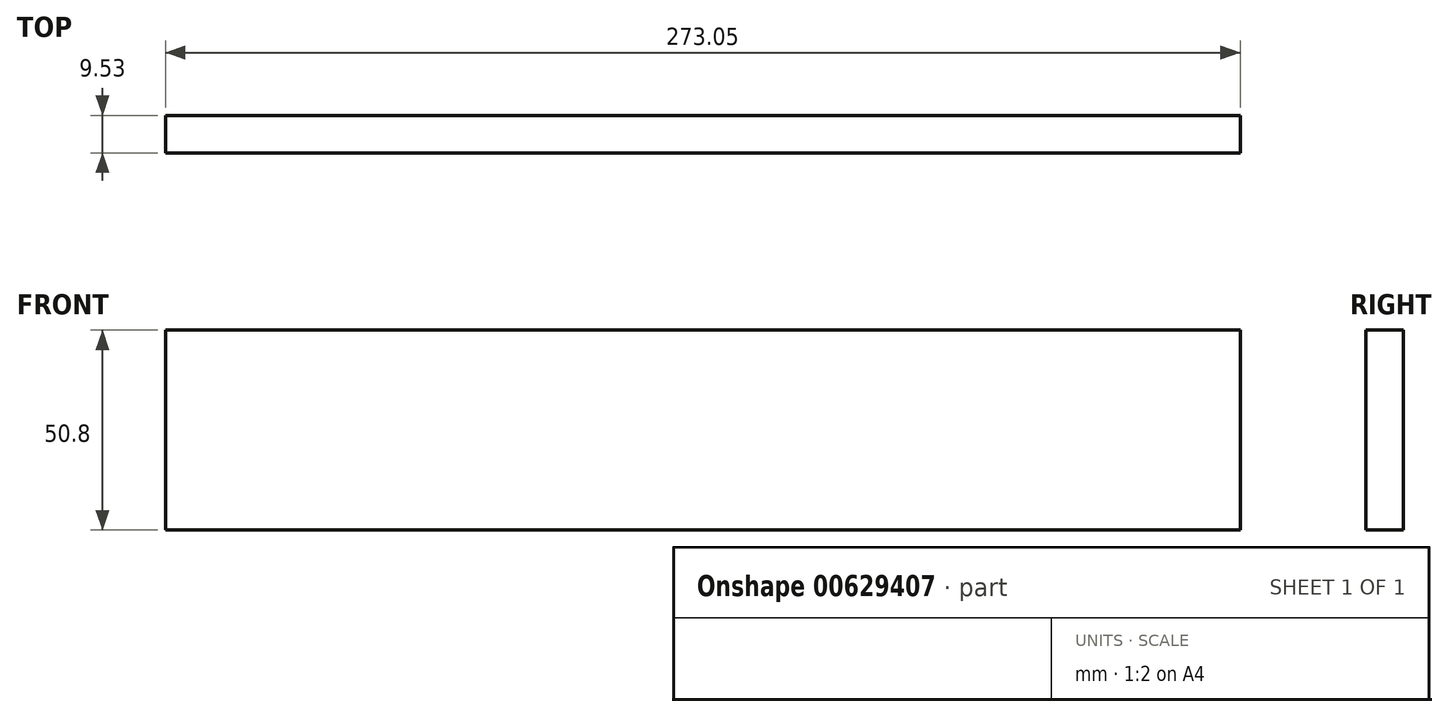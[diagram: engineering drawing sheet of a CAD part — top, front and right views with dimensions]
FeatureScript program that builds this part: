
annotation { "Feature Type Name" : "Feature", "Feature Type Description" : "" }
export const myFeature = defineFeature(function(context is Context, id is Id, definition is map)
    precondition{}
    {
        {
            var Q0;
            Q0=qCreatedBy(makeId("Front.planeOp"),FACE);
            var sketch = newSketch(context, id + "F0", { "sketchPlane" : qUnion([Q0])});
            skLineSegment(sketch, "E0.bottom", {"start": v(0, 0) * mm, "end": v(273.05, 0) * mm});
            skLineSegment(sketch, "E0.top", {"start": v(0, 50.8) * mm, "end": v(273.05, 50.8) * mm});
            skLineSegment(sketch, "E0.left", {"start": v(0, 0) * mm, "end": v(0, 50.8) * mm});
            skLineSegment(sketch, "E0.right", {"start": v(273.05, 0) * mm, "end": v(273.05, 50.8) * mm});
            skSolve(sketch);
        }
        {
            var Q0;
            Q0=qSketchRegion(id+"F0",true);
            extrude(context, id + "F1", {"entities" : qUnion([Q0]), "depth" : 9.52 * mm, "offsetDistance" : 25.4 * mm});
        }
    });
